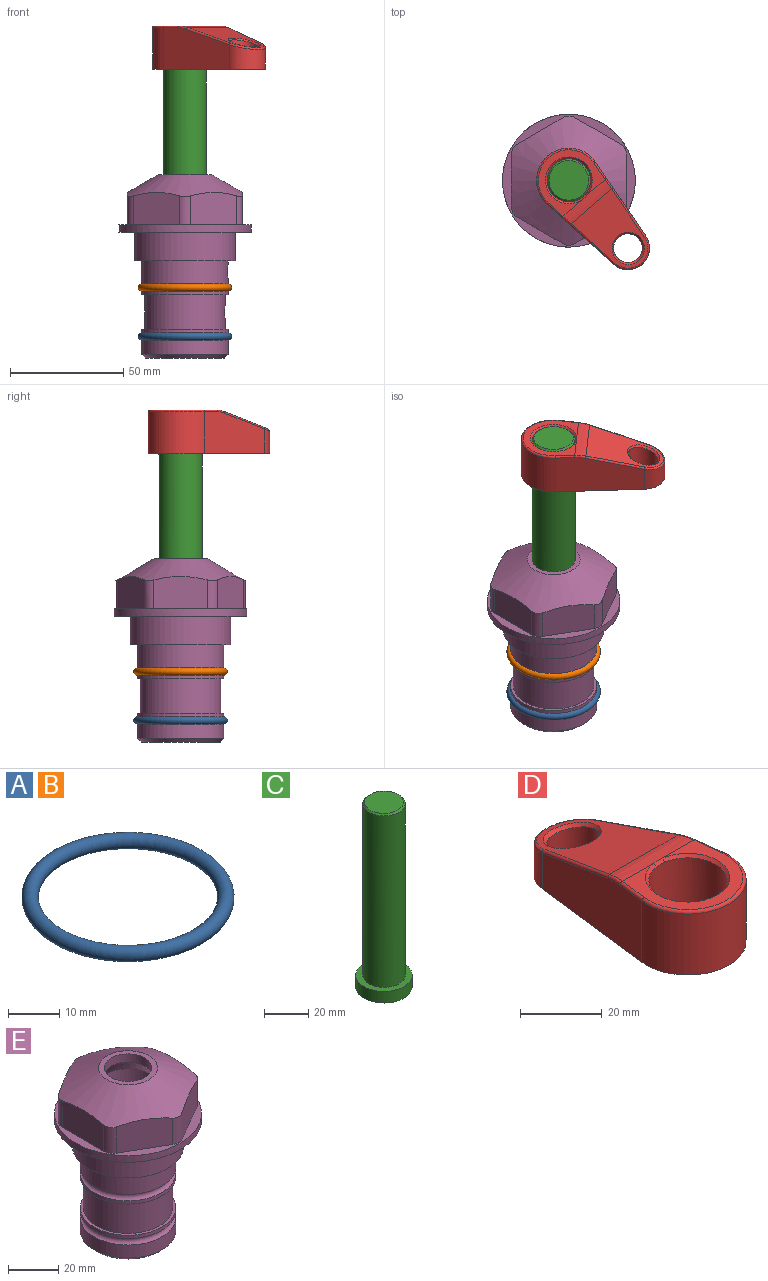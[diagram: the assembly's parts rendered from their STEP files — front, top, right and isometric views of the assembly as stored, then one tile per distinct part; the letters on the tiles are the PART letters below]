
ASSEMBLY  parts=5 mates=4
PART A: 1 faces, bbox 44.7x44.7x3.2 mm
  f0: torus R=19.05mm, axis (0,0,1), area 1193.9mm2
PART B: same geometry as A
PART C: 6 faces, bbox 25.4x25.4x101.6 mm
  f0: plane 17.46x17.46mm, normal (0,0,1), area 239.5mm2, adj f5
  f1: plane 25.4x25.4mm, normal (0,0,-1), area 506.7mm2, adj f2
  f2: cylinder r=12.7mm len=25.4mm, axis (0,0,1), area 506.7mm2, adj f1,f3
  f3: plane 25.4x25.4mm, normal (0,0,1), area 221.7mm2, adj f2,f4
  f4: cylinder r=9.53mm len=94.46mm, axis (0,0,1), area 5653mm2, adj f3,f5
  f5: cone r=8.73mm half-angle=45deg, axis (0,0,-1), area 64.4mm2, adj f0,f4
PART D: 31 faces, bbox 31.7x65.5x19.8 mm
  f0: plane 39.12x18.26mm, normal (0.99,0.12,0), area 612.2mm2, adj f1,f4,f7,f11,f13,f15
  f1: cylinder r=9.53mm len=18.91mm, axis (0,0,-1), area 296.1mm2, adj f0,f2,f7,f17
  f2: plane 39.12x18.26mm, normal (-0.99,0.12,0), area 612.2mm2, adj f1,f4,f7,f12,f14,f16
  f3: cylinder r=6.35mm len=12.7mm, axis (0,0,-1), area 362.4mm2, adj f7,f18
  f4: cylinder r=14.29mm len=28.58mm, axis (0,0,-1), area 882.2mm2, adj f0,f2,f7,f10
  f5: cylinder r=9.53mm len=19.05mm, axis (0,0,-1), area 1092.6mm2, adj f7,f19,f20
  f6: plane 26.99x23.69mm, normal (0,0,1), area 216.2mm2, adj f9,f10,f11,f12,f19
  f7: plane 63.5x28.58mm, normal (0,0,-1), area 661.8mm2, adj f0,f1,f2,f3,f4,f5,f22,f23
  f8: plane 33.52x23.6mm, normal (0,0.26,0.97), area 486mm2, adj f9,f15,f16,f17,f18
  f9: cylinder r=19.05mm len=24.72mm, axis (1,0,0), area 120.4mm2, adj f6,f8,f13,f14,f20
  f10: torus R=13.49mm, axis (0,0,1), area 59mm2, adj f4,f6,f11,f12
  f11: cylinder r=0.79mm len=8.67mm, axis (0.12,-0.99,0), area 10.8mm2, adj f0,f6,f10,f13
  f12: cylinder r=0.79mm len=8.67mm, axis (0.12,0.99,0), area 10.8mm2, adj f2,f6,f10,f14
  f13: bspline ~4.95x1.42mm, area 6.1mm2, adj f0,f9,f11,f15
  f14: bspline ~4.95x1.42mm, area 6.1mm2, adj f2,f9,f12,f16
  f15: cylinder r=0.79mm len=25.95mm, axis (0.12,-0.96,0.26), area 32.9mm2, adj f0,f8,f13,f17
  f16: cylinder r=0.79mm len=25.95mm, axis (0.12,0.96,-0.26), area 32.9mm2, adj f2,f8,f14,f17
  f17: bspline ~18.91x8.38mm, area 30mm2, adj f1,f8,f15,f16
  f18: bspline ~14.29x14.29mm, area 48.3mm2, adj f3,f8
  f19: cone r=9.53mm half-angle=45deg, axis (0,0,1), area 66.5mm2, adj f5,f6,f20
  f20: bspline ~3.22x0.96mm, area 3.5mm2, adj f5,f9,f19
  f21: plane 2.75x2.72mm, normal (0,0,-1), area 2.9mm2, adj f23,f25,f28
  f22: plane 23.05x15.88mm, normal (-0.99,-0.12,0), area 323.6mm2, adj f7,f25,f26,f27,f28,f29
  f23: plane 23.05x15.88mm, normal (0.99,-0.12,0), area 323.6mm2, adj f7,f21,f25,f27,f28,f30
  f24: cylinder r=9.53mm len=10.69mm, axis (0,0,-1), area 114.7mm2, adj f7,f27,f29,f30
  f25: cylinder r=12.7mm len=20.59mm, axis (0,0,-1), area 381.1mm2, adj f7,f21,f22,f23,f26,f28
  f26: plane 2.75x2.72mm, normal (0,0,-1), area 2.9mm2, adj f22,f25,f28
  f27: plane 19.72x18.37mm, normal (0,-0.26,-0.97), area 291.8mm2, adj f22,f23,f24,f28,f29,f30
  f28: cylinder r=15.88mm len=19.92mm, axis (1,0,0), area 54.8mm2, adj f21,f22,f23,f25,f26,f27
  f29: cylinder r=1.59mm len=11mm, axis (0,0,-1), area 34.7mm2, adj f7,f22,f24,f27
  f30: cylinder r=1.59mm len=11mm, axis (0,0,-1), area 34.7mm2, adj f7,f23,f24,f27
PART E: 36 faces, bbox 58.7x58.7x81 mm
  f0: cylinder r=17.78mm len=35.56mm, axis (0,0,1), area 1670.8mm2, adj f23,f24,f31
  f1: cylinder r=19.05mm len=38.1mm, axis (0,0,1), area 1191.9mm2, adj f26,f27,f30
  f2: plane 58.66x58.66mm, normal (0,0,-1), area 1150.6mm2, adj f3,f28
  f3: cylinder r=29.33mm len=58.66mm, axis (0,0,-1), area 585.1mm2, adj f2,f4
  f4: plane 58.66x58.66mm, normal (0,0,1), area 475.9mm2, adj f3,f5,f6,f7,f8,f9,f10,f11
  f5: plane 20.32x14.34mm, normal (-0.5,0.87,0), area 324.4mm2, adj f4,f15,f16,f17
  f6: plane 20.32x14.34mm, normal (0.5,0.87,0), area 324.4mm2, adj f4,f14,f15,f17
  f7: plane 23.48x14.34mm, normal (1,0,0), area 324.4mm2, adj f4,f13,f14,f17
  f8: plane 20.32x14.34mm, normal (0.5,-0.87,0), area 324.4mm2, adj f4,f12,f13,f17
  f9: plane 20.32x14.34mm, normal (-0.5,-0.87,0), area 324.4mm2, adj f4,f11,f12,f17
  f10: plane 23.48x14.34mm, normal (-1,0,0), area 324.4mm2, adj f4,f11,f16,f17
  f11: cylinder r=5.08mm len=12.85mm, axis (0,0,-1), area 67.2mm2, adj f4,f9,f10,f17
  f12: cylinder r=5.08mm len=12.85mm, axis (0,0,-1), area 67.2mm2, adj f4,f8,f9,f17
  f13: cylinder r=5.08mm len=12.85mm, axis (0,0,-1), area 67.2mm2, adj f4,f7,f8,f17
  f14: cylinder r=5.08mm len=12.85mm, axis (0,0,-1), area 67.2mm2, adj f4,f6,f7,f17
  f15: cylinder r=5.08mm len=12.85mm, axis (0,0,-1), area 67.2mm2, adj f4,f5,f6,f17
  f16: cylinder r=5.08mm len=12.85mm, axis (0,0,-1), area 67.2mm2, adj f4,f5,f10,f17
  f17: cone r=11.73mm half-angle=60deg, axis (0,0,-1), area 2071.8mm2, adj f5,f6,f7,f8,f9,f10,f11,f12
  f18: plane 23.46x23.46mm, normal (0,0,1), area 147.4mm2, adj f17,f35
  f19: plane 34.93x34.93mm, normal (0,0,-1), area 958mm2, adj f29
  f20: cylinder r=19.05mm len=38.1mm, axis (0,0,1), area 760.1mm2, adj f21,f29
  f21: torus R=19.05mm, axis (0,0,1), area 565.3mm2, adj f20,f22
  f22: cylinder r=19.05mm len=38.1mm, axis (0,0,1), area 190mm2, adj f21,f23
  f23: plane 38.1x38.1mm, normal (0,0,1), area 146.9mm2, adj f0,f22
  f24: plane 38.1x38.1mm, normal (0,0,-1), area 146.9mm2, adj f0,f25
  f25: cylinder r=19.05mm len=38.1mm, axis (0,0,1), area 190mm2, adj f24,f26
  f26: torus R=19.05mm, axis (0,0,1), area 565.3mm2, adj f1,f25
  f27: plane 44.45x44.45mm, normal (0,0,-1), area 411.7mm2, adj f1,f28
  f28: cylinder r=22.23mm len=44.45mm, axis (0,0,1), area 1773.5mm2, adj f2,f27
  f29: cone r=19.05mm half-angle=45deg, axis (0,0,1), area 257.5mm2, adj f19,f20
  f30: cylinder r=3.17mm len=6.75mm, axis (-1,0,0), area 128mm2, adj f1,f33
  f31: cylinder r=3.17mm len=6.35mm, axis (-1,0,0), area 102.5mm2, adj f0,f33
  f32: plane 25.4x25.4mm, normal (0,0,1), area 506.7mm2, adj f33
  f33: cylinder r=12.7mm len=66.42mm, axis (0,0,-1), area 5236.2mm2, adj f30,f31,f32,f34
  f34: cone r=9.53mm half-angle=30deg, axis (0,0,-1), area 443.4mm2, adj f33,f35
  f35: cylinder r=9.53mm len=19.05mm, axis (0,0,-1), area 240.9mm2, adj f18,f34
PLACE A t=(0,0,-21.59)mm
PLACE B at identity
PLACE C rot(axis=(0,0,-1),138.9deg) t=(0,0,27.55)mm
PLACE D rot(axis=(0,0,-1),138.9deg) t=(0,0,27.55)mm
PLACE E at identity fixed
MATE fastened A.f0 <-> E.f0  axis (0,0,1) through (0,0,-46.1)mm
MATE fastened C.f2 <-> D.f4  axis (0,0,1) through (0,0,91.05)mm
MATE fastened E.f0 <-> B.f0  axis (0,0,1) through (0,0,-24.51)mm
MATE cylindrical E.f0 <-> C.f2  axis (0,0,1) through (0,0,-50.55)mm
